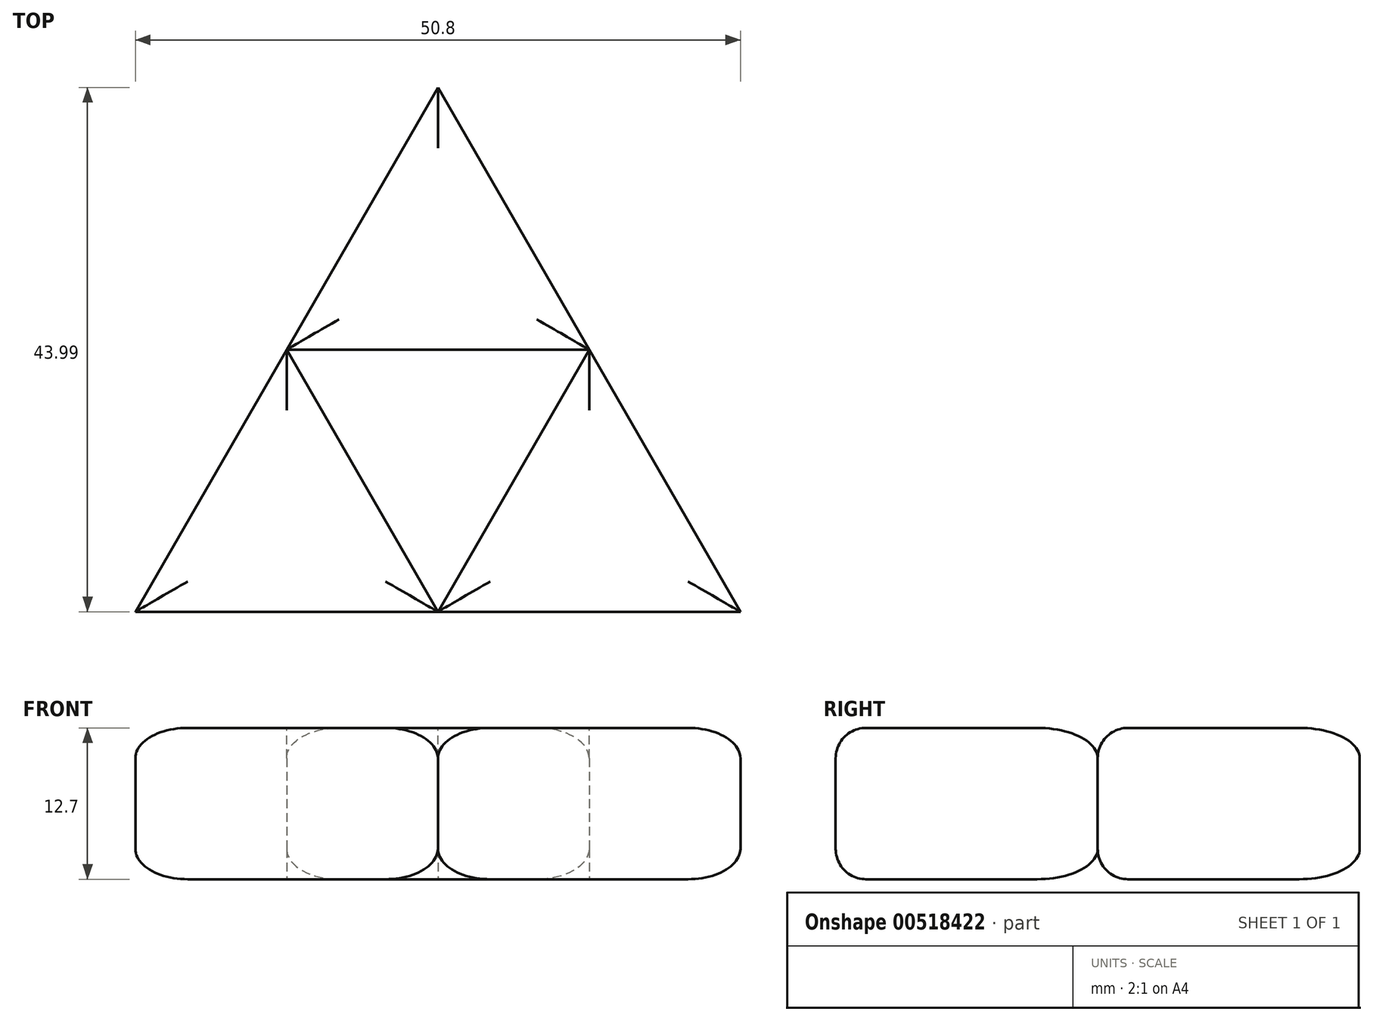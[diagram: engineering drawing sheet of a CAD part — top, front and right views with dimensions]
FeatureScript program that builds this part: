
annotation { "Feature Type Name" : "Feature", "Feature Type Description" : "" }
export const myFeature = defineFeature(function(context is Context, id is Id, definition is map)
    precondition{}
    {
        {
            var Q0;
            Q0=qCreatedBy(makeId("Top.planeOp"),FACE);
            var sketch = newSketch(context, id + "F0", { "sketchPlane" : qUnion([Q0])});
            skLineSegment(sketch, "E0", {"start": v(0, 0) * mm, "end": v(50.8, 0) * mm});
            skLineSegment(sketch, "E1", {"start": v(0, 0) * mm, "end": v(25.4, 44) * mm});
            skLineSegment(sketch, "E2", {"start": v(25.4, 44) * mm, "end": v(50.8, 0) * mm});
            skLineSegment(sketch, "E3", {"start": v(12.7, 22) * mm, "end": v(38.1, 22) * mm});
            skLineSegment(sketch, "E4", {"start": v(12.7, 22) * mm, "end": v(25.4, 0) * mm});
            skLineSegment(sketch, "E5", {"start": v(25.4, 0) * mm, "end": v(38.1, 22) * mm});
            skSolve(sketch);
        }
        {
            var Q0;
            {var subQ3=sQuery(id+"F0.wireOp",EDGE,"E3");Q0=makeQuery(id+"F0.imprint","IMPRINT",FACE,{"disambiguationData":[TD([[makeQuery(id+"F0.imprint","IMPRINT",EDGE,{"derivedFrom":subQ3}),1.0]])]});}
            var Q1;
            {var subQ3=sQuery(id+"F0.wireOp",EDGE,"E4");Q1=makeQuery(id+"F0.imprint","IMPRINT",FACE,{"disambiguationData":[TD([[makeQuery(id+"F0.imprint","IMPRINT",EDGE,{"derivedFrom":subQ3}),-1.0]])]});}
            var Q2;
            {var subQ3=sQuery(id+"F0.wireOp",EDGE,"E5");Q2=makeQuery(id+"F0.imprint","IMPRINT",FACE,{"disambiguationData":[TD([[makeQuery(id+"F0.imprint","IMPRINT",EDGE,{"derivedFrom":subQ3}),-1.0]])]});}
            extrude(context, id + "F1", {"entities" : qUnion([Q0, Q1, Q2]), "depth" : 12.7 * mm, "offsetDistance" : 25.4 * mm});
        }
        {
            var Q0;
            {var subQ0=sQuery(id+"F0.wireOp",EDGE,"E0");Q0=makeQuery(id+"F1.opExtrude","CAP_EDGE",EDGE,{"disambiguationData":[OSD([subQ0]),TDD([makeQuery(id+"F0.imprint","IMPRINT",EDGE,{"disambiguationData":[TD([[makeQuery(id+"F0.imprint","INTERSECT",VERTEX,{"derivedFrom":[subQ0,sQuery(id+"F0.wireOp",EDGE,"E2")]}),1.0]])],"derivedFrom":subQ0})])],"isStart":false});}
            var Q1;
            {var subQ0=sQuery(id+"F0.wireOp",EDGE,"E2");Q1=makeQuery(id+"F1.opExtrude","CAP_EDGE",EDGE,{"disambiguationData":[OSD([subQ0]),TDD([makeQuery(id+"F0.imprint","IMPRINT",EDGE,{"disambiguationData":[TD([[makeQuery(id+"F0.imprint","INTERSECT",VERTEX,{"derivedFrom":[sQuery(id+"F0.wireOp",EDGE,"E0"),subQ0]}),1.0]])],"derivedFrom":subQ0})])],"isStart":false});}
            var Q2;
            {var subQ0=sQuery(id+"F0.wireOp",EDGE,"E0");Q2=makeQuery(id+"F1.opExtrude","CAP_EDGE",EDGE,{"disambiguationData":[OSD([subQ0]),TDD([makeQuery(id+"F0.imprint","IMPRINT",EDGE,{"disambiguationData":[TD([[makeQuery(id+"F0.imprint","INTERSECT",VERTEX,{"derivedFrom":[subQ0,sQuery(id+"F0.wireOp",EDGE,"E1")]}),-1.0]])],"derivedFrom":subQ0})])],"isStart":false});}
            var Q3;
            Q3=makeQuery(id+"F1.opExtrude","CAP_EDGE",EDGE,{"disambiguationData":[OSD([sQuery(id+"F0.wireOp",EDGE,"E4")])],"isStart":false});
            var Q4;
            {var subQ0=sQuery(id+"F0.wireOp",EDGE,"E1");Q4=makeQuery(id+"F1.opExtrude","CAP_EDGE",EDGE,{"disambiguationData":[OSD([subQ0]),TDD([makeQuery(id+"F0.imprint","IMPRINT",EDGE,{"disambiguationData":[TD([[makeQuery(id+"F0.imprint","INTERSECT",VERTEX,{"derivedFrom":[sQuery(id+"F0.wireOp",EDGE,"E0"),subQ0]}),-1.0]])],"derivedFrom":subQ0})])],"isStart":false});}
            var Q5;
            Q5=makeQuery(id+"F1.opExtrude","CAP_EDGE",EDGE,{"disambiguationData":[OSD([sQuery(id+"F0.wireOp",EDGE,"E3")])],"isStart":false});
            var Q6;
            {var subQ0=sQuery(id+"F0.wireOp",EDGE,"E1");Q6=makeQuery(id+"F1.opExtrude","CAP_EDGE",EDGE,{"disambiguationData":[OSD([subQ0]),TDD([makeQuery(id+"F0.imprint","IMPRINT",EDGE,{"disambiguationData":[TD([[makeQuery(id+"F0.imprint","INTERSECT",VERTEX,{"derivedFrom":[subQ0,sQuery(id+"F0.wireOp",EDGE,"E2")]}),1.0]])],"derivedFrom":subQ0})])],"isStart":false});}
            var Q7;
            {var subQ0=sQuery(id+"F0.wireOp",EDGE,"E2");Q7=makeQuery(id+"F1.opExtrude","CAP_EDGE",EDGE,{"disambiguationData":[OSD([subQ0]),TDD([makeQuery(id+"F0.imprint","IMPRINT",EDGE,{"disambiguationData":[TD([[makeQuery(id+"F0.imprint","INTERSECT",VERTEX,{"derivedFrom":[sQuery(id+"F0.wireOp",EDGE,"E1"),subQ0]}),-1.0]])],"derivedFrom":subQ0})])],"isStart":false});}
            var Q8;
            {var subQ0=sQuery(id+"F0.wireOp",EDGE,"E0");Q8=makeQuery(id+"F1.opExtrude","CAP_EDGE",EDGE,{"disambiguationData":[OSD([subQ0]),TDD([makeQuery(id+"F0.imprint","IMPRINT",EDGE,{"disambiguationData":[TD([[makeQuery(id+"F0.imprint","INTERSECT",VERTEX,{"derivedFrom":[subQ0,sQuery(id+"F0.wireOp",EDGE,"E2")]}),1.0]])],"derivedFrom":subQ0})])],"isStart":true});}
            var Q9;
            {var subQ0=sQuery(id+"F0.wireOp",EDGE,"E0");Q9=makeQuery(id+"F1.opExtrude","CAP_EDGE",EDGE,{"disambiguationData":[OSD([subQ0]),TDD([makeQuery(id+"F0.imprint","IMPRINT",EDGE,{"disambiguationData":[TD([[makeQuery(id+"F0.imprint","INTERSECT",VERTEX,{"derivedFrom":[subQ0,sQuery(id+"F0.wireOp",EDGE,"E1")]}),-1.0]])],"derivedFrom":subQ0})])],"isStart":true});}
            var Q10;
            Q10=makeQuery(id+"F1.opExtrude","CAP_EDGE",EDGE,{"disambiguationData":[OSD([sQuery(id+"F0.wireOp",EDGE,"E5")])],"isStart":true});
            var Q11;
            {var subQ0=sQuery(id+"F0.wireOp",EDGE,"E1");Q11=makeQuery(id+"F1.opExtrude","CAP_EDGE",EDGE,{"disambiguationData":[OSD([subQ0]),TDD([makeQuery(id+"F0.imprint","IMPRINT",EDGE,{"disambiguationData":[TD([[makeQuery(id+"F0.imprint","INTERSECT",VERTEX,{"derivedFrom":[subQ0,sQuery(id+"F0.wireOp",EDGE,"E2")]}),1.0]])],"derivedFrom":subQ0})])],"isStart":true});}
            var Q12;
            {var subQ0=sQuery(id+"F0.wireOp",EDGE,"E1");Q12=makeQuery(id+"F1.opExtrude","CAP_EDGE",EDGE,{"disambiguationData":[OSD([subQ0]),TDD([makeQuery(id+"F0.imprint","IMPRINT",EDGE,{"disambiguationData":[TD([[makeQuery(id+"F0.imprint","INTERSECT",VERTEX,{"derivedFrom":[sQuery(id+"F0.wireOp",EDGE,"E0"),subQ0]}),-1.0]])],"derivedFrom":subQ0})])],"isStart":true});}
            var Q13;
            Q13=makeQuery(id+"F1.opExtrude","CAP_EDGE",EDGE,{"disambiguationData":[OSD([sQuery(id+"F0.wireOp",EDGE,"E5")])],"isStart":false});
            var Q14;
            {var subQ0=sQuery(id+"F0.wireOp",EDGE,"E2");Q14=makeQuery(id+"F1.opExtrude","CAP_EDGE",EDGE,{"disambiguationData":[OSD([subQ0]),TDD([makeQuery(id+"F0.imprint","IMPRINT",EDGE,{"disambiguationData":[TD([[makeQuery(id+"F0.imprint","INTERSECT",VERTEX,{"derivedFrom":[sQuery(id+"F0.wireOp",EDGE,"E0"),subQ0]}),1.0]])],"derivedFrom":subQ0})])],"isStart":true});}
            var Q15;
            {var subQ0=sQuery(id+"F0.wireOp",EDGE,"E2");Q15=makeQuery(id+"F1.opExtrude","CAP_EDGE",EDGE,{"disambiguationData":[OSD([subQ0]),TDD([makeQuery(id+"F0.imprint","IMPRINT",EDGE,{"disambiguationData":[TD([[makeQuery(id+"F0.imprint","INTERSECT",VERTEX,{"derivedFrom":[sQuery(id+"F0.wireOp",EDGE,"E1"),subQ0]}),-1.0]])],"derivedFrom":subQ0})])],"isStart":true});}
            var Q16;
            Q16=makeQuery(id+"F1.opExtrude","CAP_EDGE",EDGE,{"disambiguationData":[OSD([sQuery(id+"F0.wireOp",EDGE,"E3")])],"isStart":true});
            var Q17;
            Q17=makeQuery(id+"F1.opExtrude","CAP_EDGE",EDGE,{"disambiguationData":[OSD([sQuery(id+"F0.wireOp",EDGE,"E4")])],"isStart":true});
            fillet(context, id + "F2", {"entities" : qUnion([Q0, Q1, Q2, Q3, Q4, Q5, Q6, Q7, Q8, Q9, Q10, Q11, Q12, Q13, Q14, Q15, Q16, Q17]), "radius" : 2.54 * mm, "tangentPropagation" : true, "allowEdgeOverflow" : false});
        }
    });
